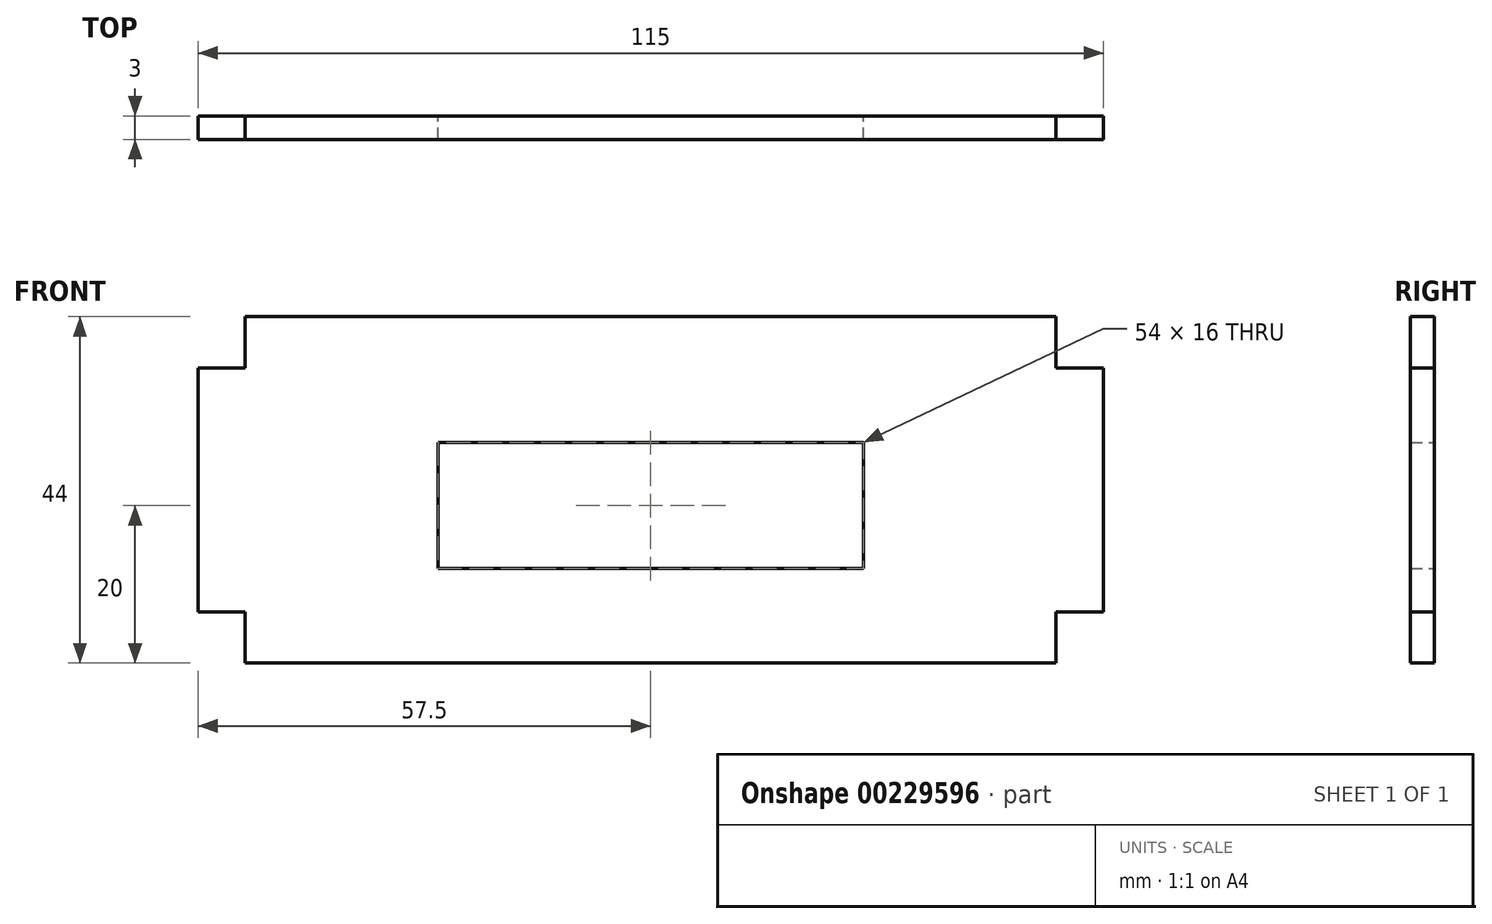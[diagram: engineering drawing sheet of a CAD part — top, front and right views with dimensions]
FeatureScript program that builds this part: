
annotation { "Feature Type Name" : "Feature", "Feature Type Description" : "" }
export const myFeature = defineFeature(function(context is Context, id is Id, definition is map)
    precondition{}
    {
        {
            var Q0;
            Q0=qCreatedBy(makeId("Front.planeOp"),FACE);
            var sketch = newSketch(context, id + "F0", { "sketchPlane" : qUnion([Q0])});
            skLineSegment(sketch, "E0.bottom", {"start": v(51.5, -22) * mm, "end": v(-51.5, -22) * mm});
            skLineSegment(sketch, "E0.top", {"start": v(51.5, 22) * mm, "end": v(-51.5, 22) * mm});
            skLineSegment(sketch, "E0.left", {"start": v(51.5, -22) * mm, "end": v(51.5, -15.5) * mm});
            skLineSegment(sketch, "E0.right", {"start": v(-51.5, -22) * mm, "end": v(-51.5, -15.5) * mm});
            skPoint(sketch, "E0.middle", {"position": v(0, 0) * mm});
            skLineSegment(sketch, "E1.bottom", {"start": v(-51.5, 15.5) * mm, "end": v(-57.5, 15.5) * mm});
            skLineSegment(sketch, "E1.top", {"start": v(-51.5, -15.5) * mm, "end": v(-57.5, -15.5) * mm});
            skLineSegment(sketch, "E1.right", {"start": v(-57.5, 15.5) * mm, "end": v(-57.5, -15.5) * mm});
            skLineSegment(sketch, "E2.MirrorCS", {"start": v(51.5, -15.5) * mm, "end": v(57.5, -15.5) * mm});
            skLineSegment(sketch, "E3.MirrorCS", {"start": v(51.5, 15.5) * mm, "end": v(57.5, 15.5) * mm});
            skLineSegment(sketch, "E4.MirrorCS", {"start": v(57.5, 15.5) * mm, "end": v(57.5, -15.5) * mm});
            skLineSegment(sketch, "E5.trimOffspring", {"start": v(-51.5, 15.5) * mm, "end": v(-51.5, 22) * mm});
            skLineSegment(sketch, "E6.trimOffspring", {"start": v(51.5, 15.5) * mm, "end": v(51.5, 22) * mm});
            skLineSegment(sketch, "E7.bottom", {"start": v(27, -10) * mm, "end": v(-27, -10) * mm});
            skLineSegment(sketch, "E7.top", {"start": v(27, 6) * mm, "end": v(-27, 6) * mm});
            skLineSegment(sketch, "E7.left", {"start": v(27, -10) * mm, "end": v(27, 6) * mm});
            skLineSegment(sketch, "E7.right", {"start": v(-27, -10) * mm, "end": v(-27, 6) * mm});
            skPoint(sketch, "E7.middle", {"position": v(0, -2) * mm});
            skSolve(sketch);
        }
        {
            var Q0;
            Q0=makeQuery(id+"F0.imprint","IMPRINT",FACE,{"disambiguationData":[TD([[makeQuery(id+"F0.imprint","IMPRINT",EDGE,{"derivedFrom":sQuery(id+"F0.wireOp",EDGE,"E0.bottom")}),-1.0]])]});
            extrude(context, id + "F1", {"entities" : qUnion([Q0]), "depth" : 3 * mm});
        }
    });
